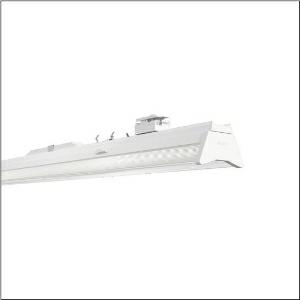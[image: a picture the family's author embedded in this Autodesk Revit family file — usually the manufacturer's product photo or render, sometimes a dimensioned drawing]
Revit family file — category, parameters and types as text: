
# Revit family: licross_r__21_performance_mo_51td16vnd65g_0ec4
name_source: partatom
category: Lighting Fixtures
units: mm (PartAtom-declared; Revit-internal decimal feet)

## family parameters
Cut with Voids When Loaded = No
Host = Face
Light Source = No
Part Type = Normal
Room Calculation Point = No
Round Connector Dimension = Use Diameter
Shared = No

## types (1)
- --- (1 x LED, 6500 lm, 38.7 W, 4000K)
    Apparent Load = 39 VA
    CIE Flux Codes = 66 88 96 79 100
    Color Rendering = 90
    Color Temperature = 4000K
    Default Elevation = 1800 mm
    Description = Licross® 21 Performance MO, luminaire insert, of sheet steel, galvanised, coil coated, white, length: 1.500mm, width: 120mm, height: 123mm, LED rated luminous flux: 6.500lm, light colour: 940, control gear: DALI 2, CLO, with plug, 5-pole, with phase selection, mains connection: 220..240V, AC, 50/60Hz, start of lifetime: 39W, end of service life: 43W, halogen-free wiring, primary light control with lens, of plastic, primary optical cover: cover, of PMMA, light emission: direct/indirect distribution, primary light characteristic: symmetric, protection rating (complete): IP54, insulation class (complete): insulation class I (protective earthing), certification: CE, ENEC, VDE, UKCA, protection symbol: D if used in an environment with non-conductive dust loads with corresponding accessories, impact resistance: IK06, permissible ambient temperature for indoor applications: -25..+40°C, corresponds to IFS (International Featured Standards) requirements for safety and quality in the food industry, reducing of maximum allowable ambient temperature of 5°C with ceiling mounting, LABS conformity tested according to VDMA 24364:2018-05, packaging unit: 1 piece
    Height = 114 mm
    Lamp = 1 x LED
    Lamp Light Flux = 6500 lm
    Lamp Power = 38.7 W
    Lamp count = 1
    Length = 1500 mm
    Luminous efficacy = 168 lm/W
    Manufacturer = Siteco
    ModVariant = No
    Model = 51TD16VND65G
    Mounting Place = Ceiling
    Mounting Type = Pendant
    Number of Poles = 1
    OnlyDefault = Yes
    Power Factor = 1
    Product Name = Licross® 21 Performance MO
    Product group = luminaire insert
    ProductGroupID = 902
    Protection Class = Protection class I
    Protection Degree = IP 54
    RLX_Detail_Level = 1
    RLX_Emergency_Light_Flux = 0 lm
    RLX_Emergency_Type = 0
    RLX_Emergency_Type_DB = No
    RlxData = <blob elided: 34045 chars, md5=87d8a476>
    Socket = socket
    Standby Power = 0 W
    System Light Flux = 6500 lm
    System Power = 39 W
    Type Comments = factory setting: luminous flux: 100 % | dim-lin: 254 | 258 mA
    Type Image = l_1256138.jpg
    URL = http://relux.com
    VarID = @adj_086138
    Voltage = 0 V
    Weight = 0.00 kg
    Width = 120 mm

## geometry (parser evidence)
native form markers: Blend x4, Sweep x13
no freeform markers — native parametric forms only
